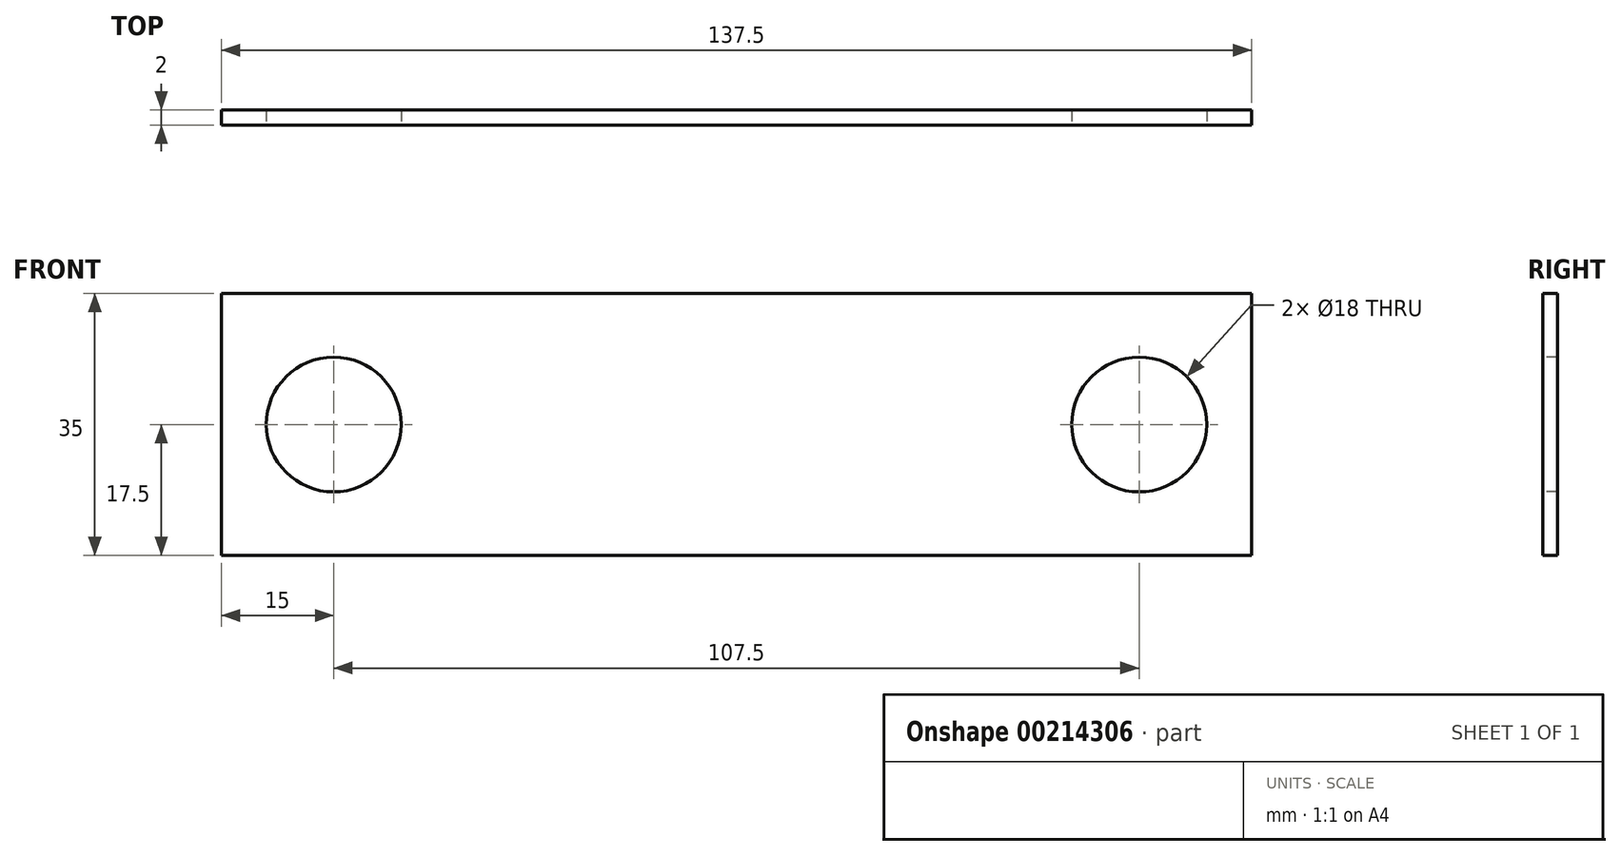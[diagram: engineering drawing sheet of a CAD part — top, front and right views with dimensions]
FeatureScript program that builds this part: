
annotation { "Feature Type Name" : "Feature", "Feature Type Description" : "" }
export const myFeature = defineFeature(function(context is Context, id is Id, definition is map)
    precondition{}
    {
        {
            var Q0;
            Q0=qCreatedBy(makeId("Front.planeOp"),FACE);
            var sketch = newSketch(context, id + "F0", { "sketchPlane" : qUnion([Q0])});
            skLineSegment(sketch, "E0.bottom", {"start": v(68.75, 17.5) * mm, "end": v(-68.75, 17.5) * mm});
            skLineSegment(sketch, "E0.top", {"start": v(68.75, -17.5) * mm, "end": v(-68.75, -17.5) * mm});
            skLineSegment(sketch, "E0.left", {"start": v(68.75, 17.5) * mm, "end": v(68.75, -17.5) * mm});
            skLineSegment(sketch, "E0.right", {"start": v(-68.75, 17.5) * mm, "end": v(-68.75, -17.5) * mm});
            skPoint(sketch, "E0.middle", {"position": v(0, 0) * mm});
            skSolve(sketch);
        }
        {
            var Q0;
            Q0=qSketchRegion(id+"F0",true);
            extrude(context, id + "F1", {"entities" : qUnion([Q0]), "depth" : 2 * mm});
        }
        {
            var Q0;
            Q0=makeQuery(id+"F1.opExtrude","CAP_FACE",FACE,{"disambiguationData":[OSD([sQuery(id+"F0.wireOp",EDGE,"E0.bottom"),sQuery(id+"F0.wireOp",EDGE,"E0.top"),sQuery(id+"F0.wireOp",EDGE,"E0.left"),sQuery(id+"F0.wireOp",EDGE,"E0.right")])],"isStart":false});
            var sketch = newSketch(context, id + "F2", { "sketchPlane" : qUnion([Q0])});
            skLineSegment(sketch, "E1.bottom", {"start": v(53.75, 0) * mm, "end": v(-53.75, 0) * mm, "construction": true});
            skLineSegment(sketch, "E1.top", {"start": v(53.75, 0) * mm, "end": v(-53.75, 0) * mm, "construction": true});
            skLineSegment(sketch, "E1.left", {"start": v(53.75, 0) * mm, "end": v(53.75, 0) * mm});
            skLineSegment(sketch, "E1.right", {"start": v(-53.75, 0) * mm, "end": v(-53.75, 0) * mm});
            skPoint(sketch, "E1.middle", {"position": v(0, 0) * mm});
            skCircle(sketch, "E2", {"center": v(-53.75, 0) * mm, "radius": 9 * mm});
            skCircle(sketch, "E3", {"center": v(53.75, 0) * mm, "radius": 9 * mm});
            skLineSegment(sketch, "E4", {"start": v(-53.75, 0) * mm, "end": v(-53.75, -17.5) * mm, "construction": true});
            skSolve(sketch);
        }
        {
            var Q0;
            Q0 = qSketchRegion(id + "F2", true);
            extrude(context, id + "F3", {"entities" : qUnion([Q0]), "operationType" : NewBodyOperationType.REMOVE, "oppositeDirection" : true, "depth" : 25 * mm});
        }
    });
